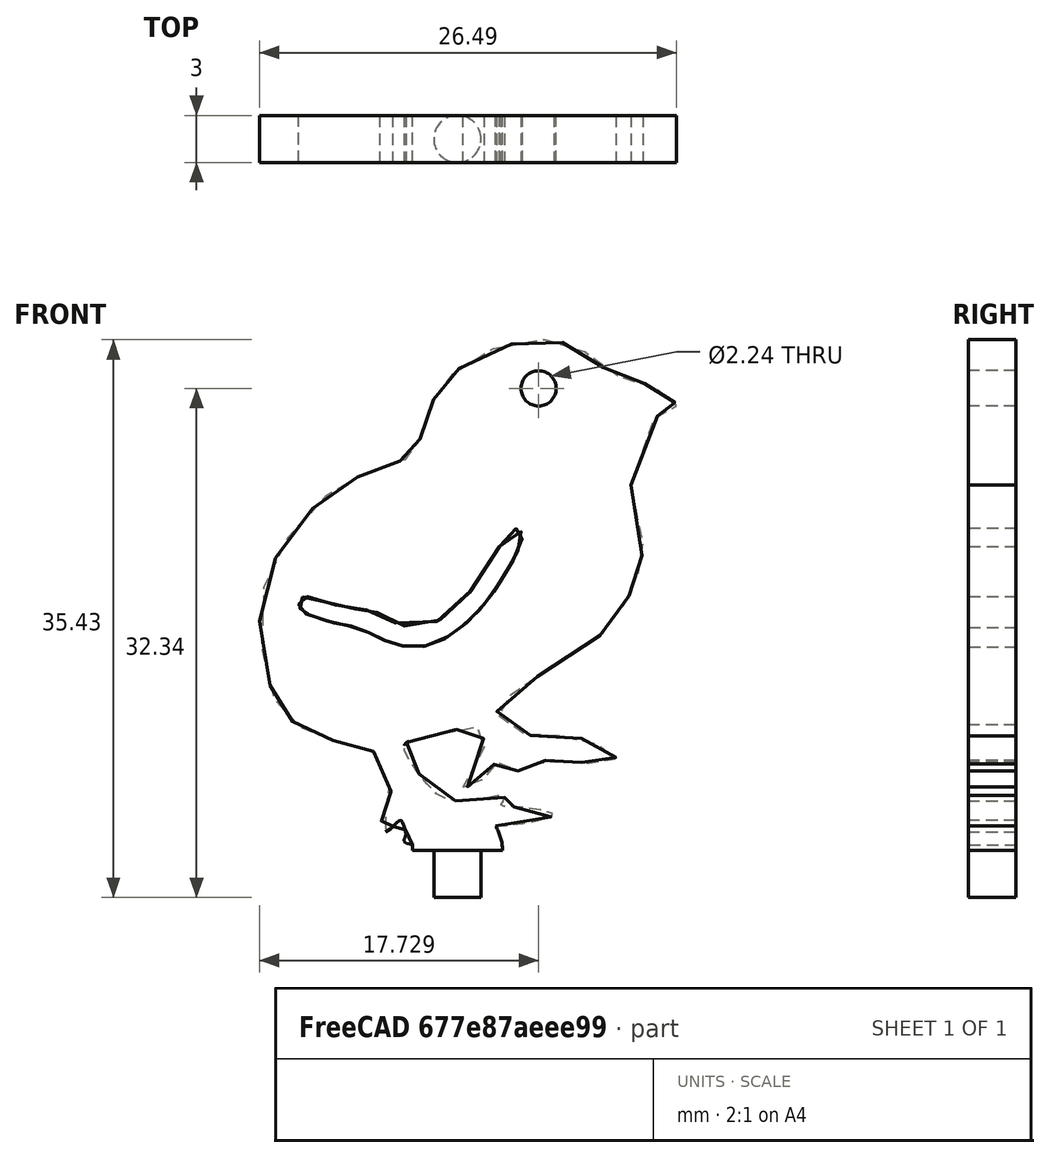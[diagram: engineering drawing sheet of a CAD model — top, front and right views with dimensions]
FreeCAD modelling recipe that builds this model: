
FCSTD DOCUMENT  (FreeCAD 0.19R)
Label: chick_2
License: All rights reserved
LicenseURL: http://en.wikipedia.org/wiki/All_rights_reserved
objects: Sketcher::SketchObject×4, PartDesign::Pad×3, Mesh::Feature×1, Part::Feature×1, PartDesign::Pocket×1, PartDesign::Body×1
note: 14 computed .brp shape members not serialized (recipe doc carries the construction recipe); baked Part::Feature solids carry a one-line shape summary decoded from their .brp

FEATURE [Mesh::Feature] chick_2
FEATURE [Part::Feature] chick_2001
  Placement = pos=(45,0,22) rot=(0,1,0;-1.5708rad)
  shape: bbox 26.56 x 1 x 32.57 mm, 3268 faces, 0 solids (baked)
FEATURE [Sketcher::SketchObject] Sketch
  FullyConstrained = false
  MapMode = 5
  Placement = pos=(0,0,0) rot=(1,0,0;1.5708rad)
  Support = -> [XZ_Plane]
  sketch-geometry (225):
    g0-g112: Circle x113 (B-spline internal-alignment scaffolding for g113; pole/knot coordinates omitted)
    g113: BSplineCurve PolesCount=113 KnotsCount=111 Degree=3 IsPeriodic=0
    g114-g224: GeomPoint x111 (B-spline internal-alignment scaffolding for g113; pole/knot coordinates omitted)
  constraints (98):
    c: Weight(g0) = 1
    c: Equal(g0,g1)
    c: Equal(g0,g2)
    c: Equal(g0,g3)
    c: PointOnObject(g3,g2)
    c: Equal(g0,g4)
    c: PointOnObject(g4,g3)
    c: Equal(g0,g5)
    c: Equal(g0,g6)
    c: PointOnObject(g6,g4)
    c: Equal(g0,g7)
    c: PointOnObject(g7,g6)
    c: Equal(g0, g8-g18) x11
    c: PointOnObject(g18,g17)
    c: Equal(g0,g19)
    c: PointOnObject(g19,g18)
    c: Equal(g0,g20)
    c: Equal(g0,g21)
    c: PointOnObject(g21,g20)
    c: Equal(g0, g22-g35) x14
    c: PointOnObject(g35,g34)
    c: Equal(g0, g36-g40) x5
    c: PointOnObject(g40,g39)
    c: Equal(g0,g41)
    c: PointOnObject(g41,g40)
    c: Equal(g0, g42-g45) x4
    c: PointOnObject(g45,g44)
    c: Equal(g0,g46)
    c: PointOnObject(g46,g44)
    c: Equal(g0,g47)
    c: Equal(g0,g48)
    c: PointOnObject(g48,g46)
    c: Equal(g0,g49)
    c: Equal(g0,g50)
    c: PointOnObject(g50,g46)
    c: Equal(g0,g51)
    c: PointOnObject(g51,g49)
    c: Equal(g0, g52-g55) x4
    c: PointOnObject(g55,g54)
    c: Equal(g0, g56-g62) x7
    c: PointOnObject(g62,g61)
    c: Equal(g0,g63)
    c: Equal(g0,g64)
    c: PointOnObject(g64,g62)
    c: Equal(g0,g65)
    c: Equal(g0,g66)
    c: PointOnObject(g66,g65)
    c: Equal(g0, g67-g71) x5
    c: PointOnObject(g71,g69)
    c: Equal(g0,g72)
    c: Equal(g0,g73)
    c: Equal(g0,g74)
    c: PointOnObject(g74,g73)
    c: Equal(g0,g75)
    c: Equal(g0,g76)
    c: Equal(g0,g77)
    c: PointOnObject(g77,g76)
    c: Equal(g0,g78)
    c: PointOnObject(g78,g77)
    c: Equal(g0,g79)
    c: PointOnObject(g79,g66)
    c: Equal(g0,g80)
    c: PointOnObject(g80,g78)
    c: Equal(g0,g81)
    c: PointOnObject(g81,g78)
    c: Equal(g0,g82)
    c: Equal(g0,g83)
    c: PointOnObject(g83,g77)
    c: Equal(g0,g84)
    c: Equal(g0,g85)
    c: Equal(g0,g86)
    c: PointOnObject(g86,g85)
    c: Equal(g0,g87)
    c: Equal(g0,g88)
    c: Equal(g0,g89)
    c: PointOnObject(g89,g88)
    c: Equal(g0,g90)
    c: Equal(g0,g91)
    c: PointOnObject(g91,g90)
    c: Equal(g0,g92)
    c: Equal(g0,g93)
    c: PointOnObject(g93,g91)
    c: Equal(g0, g94-g99) x6
    c: PointOnObject(g99,g98)
    c: Equal(g0, g100-g106) x7
    c: PointOnObject(g106,g105)
    c: Equal(g0,g107)
    c: Equal(g0,g108)
    c: PointOnObject(g108,g107)
    c: Equal(g0,g109)
    c: PointOnObject(g109,g108)
    c: Equal(g0,g110)
    c: Equal(g0,g111)
    c: Equal(g0,g112)
    c: PointOnObject(g113,g111)
    c: InternalAlignment(g0-g112 -> g113) x113
    c: InternalAlignment(g114-g224 -> g113) x111
    c: Coincident(g113,g113)
FEATURE [PartDesign::Pad] Pad
  Direction = (1,1,1)
  Length = 3
  Length2 = 100
  Placement = pos=(0,0,0) rot=(1,0,0;1.5708rad)
  Profile = -> Sketch
  Type = 0
FEATURE [Sketcher::SketchObject] Sketch001
  FullyConstrained = false
  MapMode = 5
  Placement = pos=(0,-3,2e-15) rot=(1,0,0;1.5708rad)
  Support = -> [Pad]
  sketch-geometry (94):
    g0: Circle CenterX=5.15888 CenterY=29.3397 CenterZ=0 NormalX=0 NormalY=0 NormalZ=1 AngleXU=0 Radius=1.11877
    g1-g47: Circle x47 (B-spline internal-alignment scaffolding for g48; pole/knot coordinates omitted)
    g48: BSplineCurve PolesCount=47 KnotsCount=45 Degree=3 IsPeriodic=0
    g49-g93: GeomPoint x45 (B-spline internal-alignment scaffolding for g48; pole/knot coordinates omitted)
  constraints (7):
    c: Weight(g1) = 1
    c: Equal(g1, g2-g38) x37
    c: PointOnObject(g38,g37)
    c: Equal(g1, g39-g47) x9
    c: InternalAlignment(g1-g47 -> g48) x47
    c: InternalAlignment(g49-g93 -> g48) x45
    c: Coincident(g48,g48)
FEATURE [PartDesign::Pocket] Pocket
  BaseFeature = -> Pad
  Length = 5
  Length2 = 100
  Placement = pos=(0,0,0) rot=(1,0,0;1.5708rad)
  Profile = -> Sketch001
  Type = 0
FEATURE [Sketcher::SketchObject] Sketch002
  FullyConstrained = false
  MapMode = 5
  Placement = pos=(0,-3,3.3e-15) rot=(1,0,0;1.5708rad)
  Support = -> [Pocket]
  sketch-geometry (2):
    g0: ArcOfCircle CenterX=0 CenterY=0 CenterZ=0 NormalX=0 NormalY=0 NormalZ=1 AngleXU=0 Radius=2.86396 StartAngle=0 EndAngle=3.14159
    g1: LineSegment StartX=-2.86396 StartY=4e-16 StartZ=0 EndX=2.86396 EndY=4e-16 EndZ=0
  constraints (5):
    c: Coincident(g0,g-1)
    c: PointOnObject(g0,g-1)
    c: Coincident(g1,g0)
    c: Coincident(g1,g0)
    c: Horizontal(g1)
FEATURE [PartDesign::Pad] Pad001
  BaseFeature = -> Pocket
  Direction = (1,1,1)
  Length = 3
  Length2 = 100
  Placement = pos=(0,0,0) rot=(1,0,0;1.5708rad)
  Profile = -> Sketch002
  Reversed = true
  Type = 0
FEATURE [Sketcher::SketchObject] Sketch003
  FullyConstrained = true
  MapMode = 5
  Placement = pos=(0,0,4e-16) rot=(1,0,0;3.14159rad)
  Support = -> [Pad001]
  sketch-geometry (1):
    g0: Circle CenterX=0 CenterY=1.5 CenterZ=0 NormalX=0 NormalY=0 NormalZ=1 AngleXU=0 Radius=1.5
  constraints (3):
    c: PointOnObject(g0,g-2)
    c: Diameter(g0) = 3
    c: DistanceY(g-1,g0) = 1.5
FEATURE [PartDesign::Pad] Pad002
  BaseFeature = -> Pad001
  Direction = (1,1,1)
  Length = 3
  Length2 = 100
  Placement = pos=(0,0,0) rot=(1,0,0;1.5708rad)
  Profile = -> Sketch003
  Type = 0
FEATURE [PartDesign::Body] Body
  Group = -> [Sketch,Pad,Sketch001,Pocket,Sketch002,Pad001,Sketch003,Pad002]
  Origin = -> Origin
  Tip = -> Pad002
